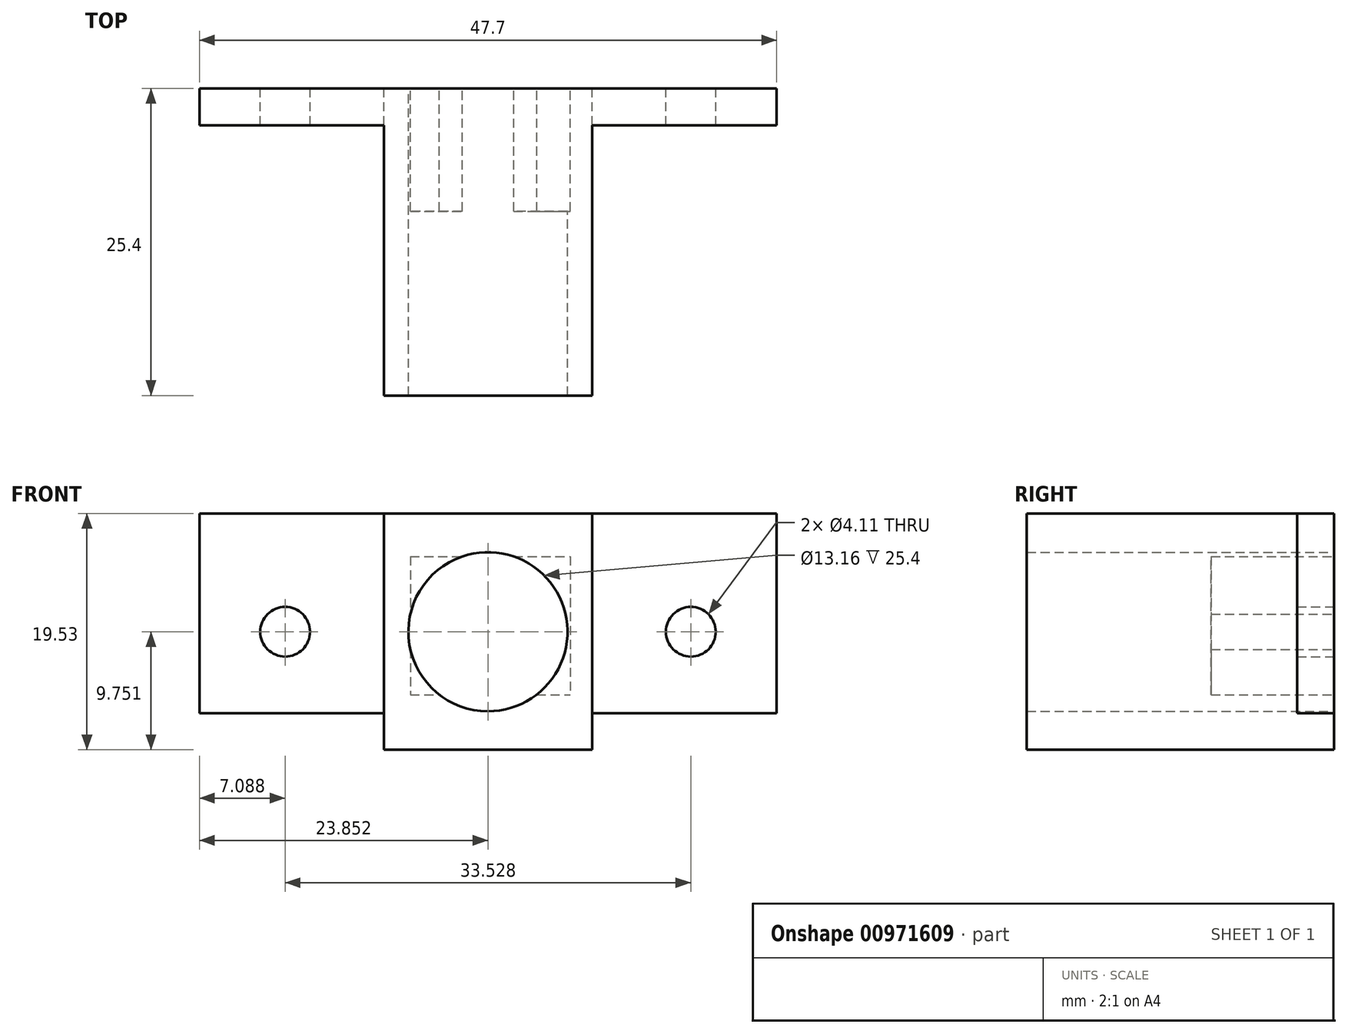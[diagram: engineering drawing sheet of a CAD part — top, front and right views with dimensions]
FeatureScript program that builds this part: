
annotation { "Feature Type Name" : "Feature", "Feature Type Description" : "" }
export const myFeature = defineFeature(function(context is Context, id is Id, definition is map)
    precondition{}
    {
        {
            var Q0;
            Q0=qCreatedBy(makeId("Front.planeOp"),FACE);
            var sketch = newSketch(context, id + "F0", { "sketchPlane" : qUnion([Q0])});
            skLineSegment(sketch, "E0", {"start": v(-40.83, 31.72) * mm, "end": v(-23.6, 31.72) * mm});
            skLineSegment(sketch, "E1", {"start": v(-40.83, 12.19) * mm, "end": v(-23.6, 12.19) * mm});
            skCircle(sketch, "E2", {"center": v(-32.22, 21.94) * mm, "radius": 6.58 * mm});
            skLineSegment(sketch, "E3", {"start": v(-40.83, 31.72) * mm, "end": v(-40.83, 12.19) * mm});
            skLineSegment(sketch, "E4", {"start": v(-23.6, 31.72) * mm, "end": v(-23.6, 12.19) * mm});
            skCircle(sketch, "E5", {"center": v(-32.22, 21.94) * mm, "radius": 2.06 * mm});
            skSolve(sketch);
        }
        {
            var Q0;
            Q0=makeQuery(id+"F0.imprint","IMPRINT",FACE,{"disambiguationData":[TD([[makeQuery(id+"F0.imprint","IMPRINT",EDGE,{"derivedFrom":sQuery(id+"F0.wireOp",EDGE,"SmfyHSjA-LpOb-Yx3U-Kuvu-dPIdQ33qvWrQ")}),-1.0]])]});
            var Q1;
            Q1=makeQuery(id+"F0.imprint","IMPRINT",FACE,{"disambiguationData":[TD([[makeQuery(id+"F0.imprint","IMPRINT",EDGE,{"derivedFrom":sQuery(id+"F0.wireOp",EDGE,"E0")}),-1.0]])]});
            extrude(context, id + "F1", {"entities" : qUnion([Q0, Q1]), "depth" : 25.4 * mm, "offsetDistance" : 25.4 * mm});
        }
        {
            var Q0;
            Q0=qCreatedBy(makeId("Front.planeOp"),FACE);
            var sketch = newSketch(context, id + "F2", { "sketchPlane" : qUnion([Q0])});
            skLineSegment(sketch, "E6", {"start": v(-40.83, 31.72) * mm, "end": v(-56.07, 31.72) * mm});
            skLineSegment(sketch, "E7", {"start": v(-40.83, 15.21) * mm, "end": v(-56.07, 15.21) * mm});
            skLineSegment(sketch, "E8", {"start": v(-56.07, 15.21) * mm, "end": v(-56.07, 31.72) * mm});
            skLineSegment(sketch, "E9", {"start": v(-23.6, 31.72) * mm, "end": v(-8.37, 31.72) * mm});
            skLineSegment(sketch, "E10", {"start": v(-8.37, 31.72) * mm, "end": v(-8.37, 15.21) * mm});
            skLineSegment(sketch, "E11", {"start": v(-8.37, 15.21) * mm, "end": v(-23.6, 15.21) * mm});
            skCircle(sketch, "E12", {"center": v(-48.98, 21.94) * mm, "radius": 2.06 * mm});
            skCircle(sketch, "E13", {"center": v(-15.45, 21.94) * mm, "radius": 2.06 * mm});
            skLineSegment(sketch, "E14", {"start": v(-23.6, 31.72) * mm, "end": v(-23.6, 15.21) * mm});
            skLineSegment(sketch, "E15", {"start": v(-40.83, 31.72) * mm, "end": v(-40.83, 15.21) * mm});
            skLineSegment(sketch, "E16.0", {"start": v(-23.6, 31.72) * mm, "end": v(-23.6, 12.19) * mm});
            skPoint(sketch, "E17.0", {"position": v(-32.22, 21.94) * mm});
            skCircle(sketch, "E18.0", {"center": v(-32.22, 21.94) * mm, "radius": 2.06 * mm});
            skLineSegment(sketch, "E19", {"start": v(-32.22, 21.94) * mm, "end": v(-15.45, 21.94) * mm, "construction": true});
            skLineSegment(sketch, "E20", {"start": v(-32.22, 21.94) * mm, "end": v(-48.98, 21.94) * mm, "construction": true});
            skSolve(sketch);
        }
        {
            var Q0;
            Q0=makeQuery(id+"F2.imprint","IMPRINT",FACE,{"disambiguationData":[TD([[makeQuery(id+"F2.imprint","IMPRINT",EDGE,{"derivedFrom":sQuery(id+"F2.wireOp",EDGE,"E9")}),-1.0]])]});
            var Q1;
            Q1=makeQuery(id+"F2.imprint","IMPRINT",FACE,{"disambiguationData":[TD([[makeQuery(id+"F2.imprint","IMPRINT",EDGE,{"derivedFrom":sQuery(id+"F2.wireOp",EDGE,"E6")}),1.0]])]});
            extrude(context, id + "F3", {"entities" : qUnion([Q0, Q1]), "operationType" : NewBodyOperationType.ADD, "depth" : 3.05 * mm, "offsetDistance" : 25.4 * mm});
        }
        {
            var Q0;
            Q0=qCreatedBy(makeId("Front.planeOp"),FACE);
            var sketch = newSketch(context, id + "F4", { "sketchPlane" : qUnion([Q0])});
            skText(sketch, "E21", { "text": "R.P.U", "fontName": "OpenSans-Bold.ttf"});
            const initialGuessF4  = {"E21": [-0.03477, 0.02956, 1, 0, 0.00168]};
            skSetInitialGuess(sketch, initialGuessF4);
            skSolve(sketch);
        }
        {
            var Q0;
            Q0 = qSketchRegion(id + "F4", true);
            extrude(context, id + "F5", {"entities" : qUnion([Q0]), "operationType" : NewBodyOperationType.ADD, "depth" : 22.86 * mm, "offsetDistance" : 25.4 * mm});
        }
        {
            var Q0;
            Q0=qCreatedBy(makeId("Front.planeOp"),FACE);
            var sketch = newSketch(context, id + "F6", { "sketchPlane" : qUnion([Q0])});
            skLineSegment(sketch, "E22", {"start": v(-38.63, 28.17) * mm, "end": v(-38.63, 16.74) * mm});
            skLineSegment(sketch, "E23", {"start": v(-38.63, 16.74) * mm, "end": v(-25.43, 16.74) * mm});
            skLineSegment(sketch, "E24", {"start": v(-38.63, 28.17) * mm, "end": v(-25.43, 28.17) * mm});
            skLineSegment(sketch, "E25", {"start": v(-25.43, 28.17) * mm, "end": v(-25.43, 16.74) * mm});
            skSolve(sketch);
        }
        {
            var Q0;
            Q0=makeQuery(id+"F6.imprint","IMPRINT",FACE,{"disambiguationData":[TD([[makeQuery(id+"F6.imprint","IMPRINT",EDGE,{"derivedFrom":sQuery(id+"F6.wireOp",EDGE,"E22")}),1.0]])]});
            extrude(context, id + "F7", {"entities" : qUnion([Q0]), "operationType" : NewBodyOperationType.REMOVE, "depth" : 10.16 * mm, "offsetDistance" : 25.4 * mm});
        }
    });
